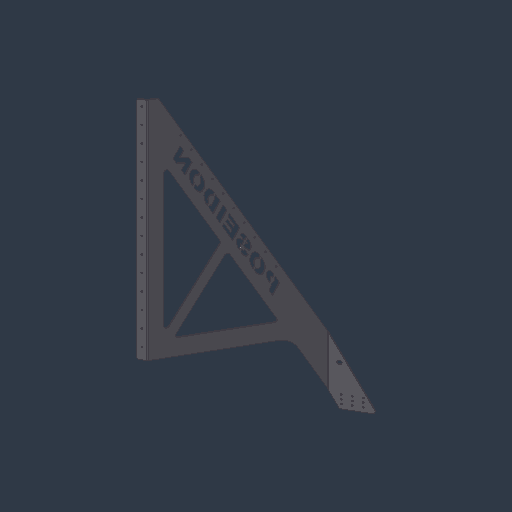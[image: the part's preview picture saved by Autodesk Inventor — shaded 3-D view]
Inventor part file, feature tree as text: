
AUTODESK INVENTOR PART (.ipt)
format: ipt  version: 2024.3 (Build 283343000, 343)  size: 1,169,408 bytes
history: native  units: mm (DEFAULTED — no unit token found)
features: other x5, plane x3, mirror x2, boolean_combine x2, hole x2, sketch x2, pattern_linear x1
ambient origin geometry x8: Origin, YZ Plane, XZ Plane, XY Plane, X Axis, Y Axis, Z Axis, Center Point
bodies: Solid2 (feature_tree), Solid7 (feature_tree), Solid8 (feature_tree)
feature tree (17):
  other  "PLATE,SIDE,BRACE,ELEVATOR.ipt"
  plane  "Work Plane6"
  mirror  "Mirror2"
  plane  "Work Plane7"
  mirror  "Mirror3"
  boolean_combine  "Combine6"
  boolean_combine  "Combine7"
  hole  "Hole3"  [1 undecoded]
  other  "Solid2::PLATE,SIDE,BRACE,ELEVATOR.ipt"
  other  "TaggingFeature1"
  plane  "Work Plane5"
  sketch  "Sketch6"  dims[d88=10.0mm d89=3.175mm]
  other  "Solid7::PLATE,SIDE,BRACE,ELEVATOR.ipt"
  other  "Solid8::PLATE,SIDE,BRACE,ELEVATOR.ipt"
  sketch  "Sketch7"  dims[d95=-396.875mm d96=19.05mm d99=20.594885mm d100=14.3117mm d101=1.9558mm d102=9.779mm d103=25.4mm d104=4.9784mm d105=50.8mm d107=100.0mm d109=117.689036mm d110=7.937424mm d113=3.175mm d114=3.175mm d115=127.0mm d116=25.4mm d117=12.7508mm d118=19.05mm d119=9.525mm d120=6.35mm d121=14.3117mm d122=3.175mm d123=20.594885mm]
  pattern_linear  "Rectangular Pattern1"  Spacing1=19.05mm  [1 undecoded]
  hole  "Hole2"  [1 undecoded]
note: 3 required parameter values undecoded (feature->parameter linkage not recoverable at this tier; creation-order binding heuristic only, values carry confidence <= 0.55)
